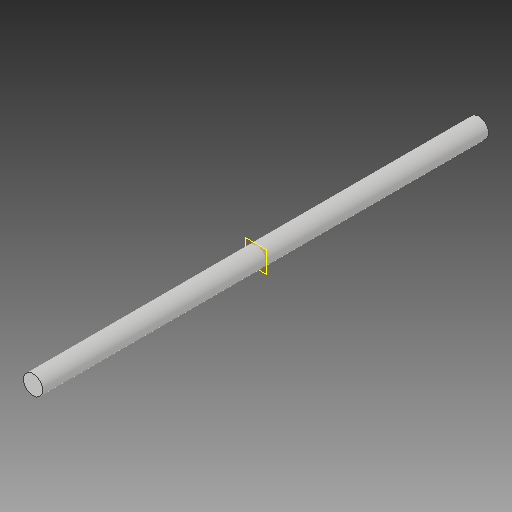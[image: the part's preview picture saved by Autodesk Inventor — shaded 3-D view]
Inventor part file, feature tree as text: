
AUTODESK INVENTOR PART (.ipt)
format: ipt  version: 2018 (Build 220112000, 112)  size: 89,088 bytes
history: native  units: mm
features: other x1, extrude x1, sketch x1
ambient origin geometry x8: Origin, YZ Plane, XZ Plane, XY Plane, X Axis, Y Axis, Z Axis, Center Point
bodies: Body1 (feature_tree)
feature tree (3):
  other  "ソリッド1"
  extrude  "押し出し1"  Depth=10.0mm
  sketch  "スケッチ1"
